# Revit family: Gelenkhalter für Profilanschluss l-q, zn
name_source: partatom
category: HLS-Bauteile
units: mm (PartAtom-declared; Revit-internal decimal feet)

## family parameters
Arbeitsebenenbasiert = Ja
Beim Laden mit Abzugskörper schneiden = Nein
Bemaßung runder Anschluss = Durchmesser verwenden
Beschriftungsausrichtung beibehalten = Nein
Gemeinsam genutzt = Ja
Immer vertikal = Nein
Raumberechnungspunkt = Nein
Teiletyp = Normal

## types (1)
- Gelenkhalter für Profilanschluss l-q, zn
    Artikelnummer = 08120601/zn
    Ausrichtung = längs/quer
    EAN = 4250928468796
    Fabrikat = MEFA
    Firma = MEFA Befestigungs- und Montagesysteme GmbH
    Gewicht = 0.82 kg
    Gewicht pro Bauteil = 0.82 kg
    Kurztext1 = Gelenkhalter C-Profil 45
    Kurztext2 = C-Profil längs/quer max. Winkel 90 ° ZnNi
    Lochdurchmesser = 13 mm
    Material = Stahl
    Materialname = S235
    Mengeneinheit = St
    Profil = C-Profil
    Profiltyp = 45
    Vorgabe-Ansicht = 1219 mm
    Winkel = 90 °
    max. zul. Last = 7.00 kN
    vpe = 10

## geometry (parser evidence)
native form markers: Sweep x1
no freeform markers — native parametric forms only
